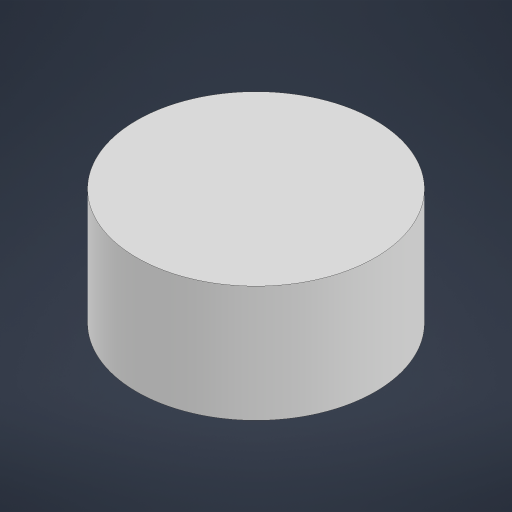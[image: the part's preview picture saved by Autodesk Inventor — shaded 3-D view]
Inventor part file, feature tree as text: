
AUTODESK INVENTOR PART (.ipt)
format: ipt  version: 2024.1 (Build 281209000, 209)  size: 142,336 bytes
history: native  units: in
note: dims shown in document units (in); Inventor stores cm internally (conversion verified against a paired STEP export)
features: extrude x1, sketch x1
ambient origin geometry x8: Origin, YZ Plane, XZ Plane, XY Plane, X Axis, Y Axis, Z Axis, Center Point
bodies: Solid1 (feature_tree)
feature tree (2):
  extrude  "Extrusion1"  [1 undecoded]
  sketch  "Sketch1"  dims[d0=1.0in d1=0.0in]
note: 1 required parameter value undecoded (feature->parameter linkage not recoverable at this tier; creation-order binding heuristic only, values carry confidence <= 0.55)
